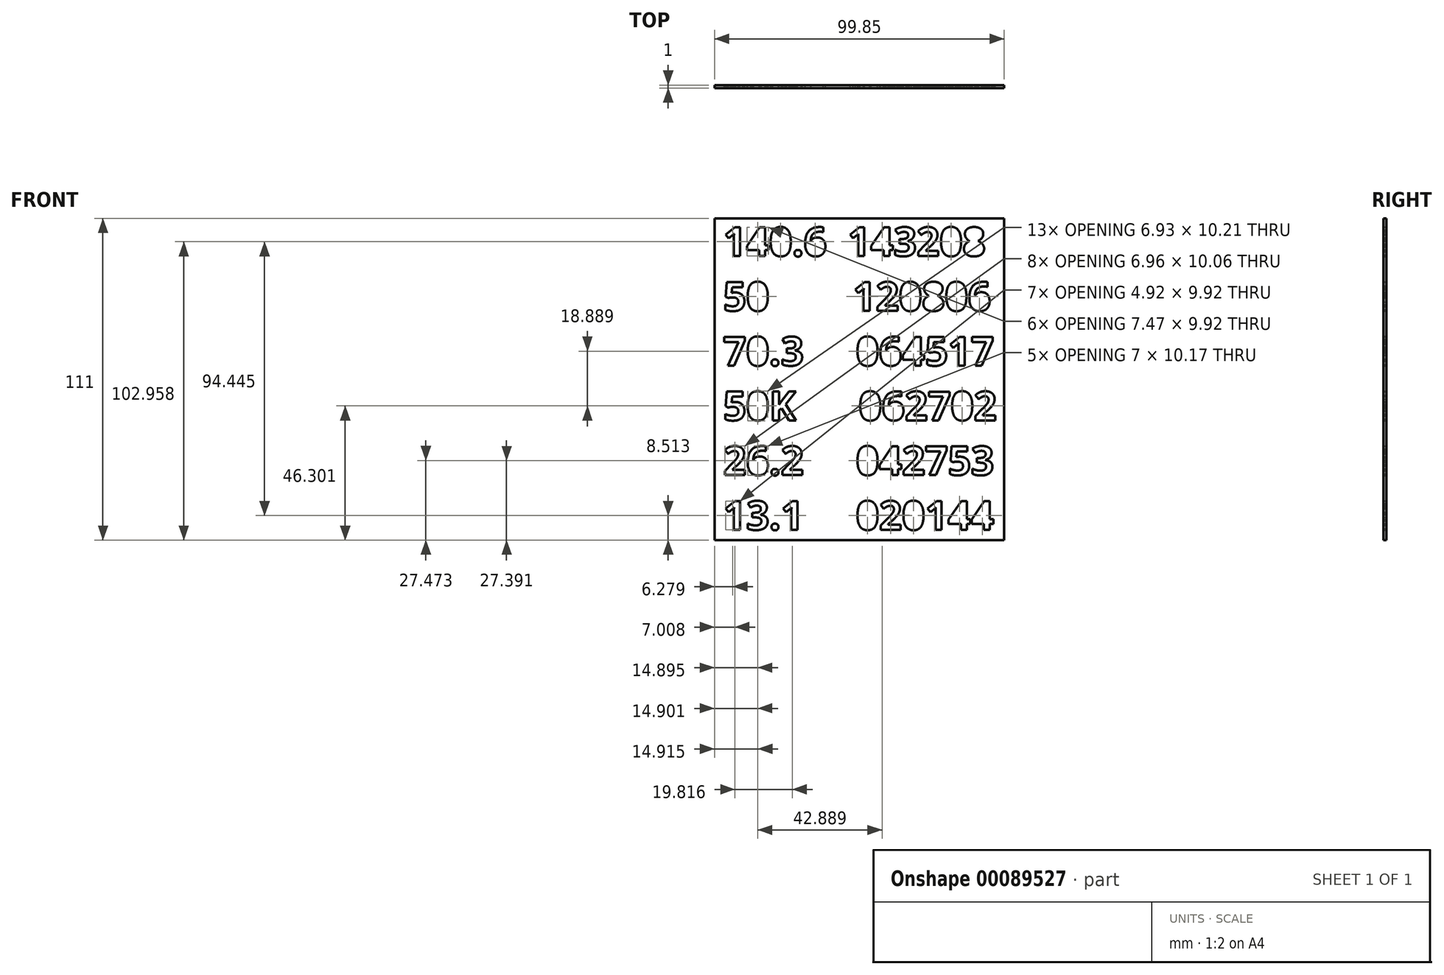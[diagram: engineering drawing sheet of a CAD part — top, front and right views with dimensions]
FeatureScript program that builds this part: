
annotation { "Feature Type Name" : "Feature", "Feature Type Description" : "" }
export const myFeature = defineFeature(function(context is Context, id is Id, definition is map)
    precondition{}
    {
        {
            var Q0;
            Q0=qCreatedBy(makeId("Front.planeOp"),FACE);
            var sketch = newSketch(context, id + "F0", { "sketchPlane" : qUnion([Q0])});
            skText(sketch, "E0", { "text": "140.6  143208\n50        120806\n70.3     064517\n50K      062702\n26.2     042753\n13.1     020144", "fontName": "OpenSans-Bold.ttf"});
            skLineSegment(sketch, "E1.bottom", {"start": v(-48.18, -7.92) * mm, "end": v(51.67, -7.92) * mm});
            skLineSegment(sketch, "E1.top", {"start": v(-48.18, -118.92) * mm, "end": v(51.67, -118.92) * mm});
            skLineSegment(sketch, "E1.left", {"start": v(-48.18, -7.92) * mm, "end": v(-48.18, -118.92) * mm});
            skLineSegment(sketch, "E1.right", {"start": v(51.67, -7.92) * mm, "end": v(51.67, -118.92) * mm});
            const initialGuessF0  = {"E0": [-0.04518, -0.02092, 1, 0, 0.01]};
            skSetInitialGuess(sketch, initialGuessF0);
            skSolve(sketch);
        }
        {
            var Q0;
            Q0=makeQuery(id+"F0.imprint","IMPRINT",FACE,{"disambiguationData":[TD([[makeQuery(id+"F0.imprint","IMPRINT",EDGE,{"derivedFrom":sQuery(id+"F0.wireOp",EDGE,"E0.sketch_text.stroke-0")}),1.0]])]});
            extrude(context, id + "F1", {"entities" : qUnion([Q0]), "depth" : 1 * mm});
        }
    });
